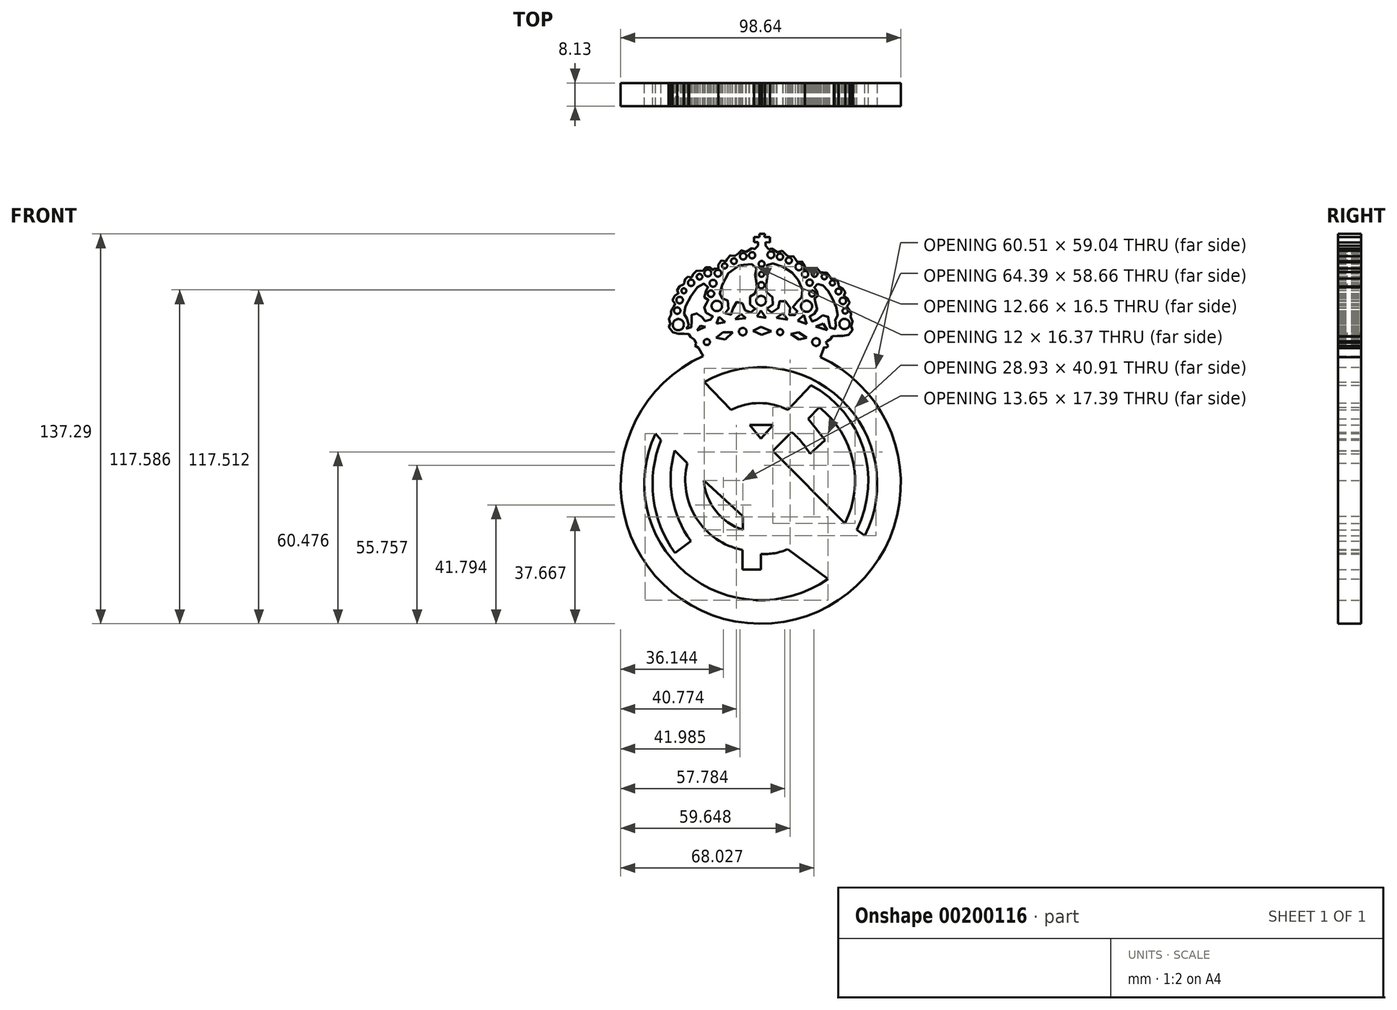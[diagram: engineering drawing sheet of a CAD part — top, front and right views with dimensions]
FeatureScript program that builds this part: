
annotation { "Feature Type Name" : "Feature", "Feature Type Description" : "" }
export const myFeature = defineFeature(function(context is Context, id is Id, definition is map)
    precondition{}
    {
        {
            var Q0;
            Q0=qCreatedBy(makeId("Front.planeOp"),FACE);
            var sketch = newSketch(context, id + "F0", { "sketchPlane" : qUnion([Q0])});
            skCircle(sketch, "E0", {"center": v(0, -1.17) * mm, "radius": 49.32 * mm});
            skCircle(sketch, "E1", {"center": v(0, -1.17) * mm, "radius": 41.02 * mm});
            skArc(sketch, "E2", {"start": v(-18.95, 33.67) * mm, "mid": v(-37.34, 6.45) * mm, "end": v(-30.16, -25.6) * mm});
            skArc(sketch, "E3", {"start": v(-19.8, 27.48) * mm, "mid": v(-31.53, 3.97) * mm, "end": v(-24.63, -21.38) * mm});
            skLineSegment(sketch, "E4", {"start": v(-19.8, 27.48) * mm, "end": v(-14.73, 21.41) * mm});
            skLineSegment(sketch, "E5", {"start": v(-18.95, 33.67) * mm, "end": v(-10.43, 24.82) * mm});
            skArc(sketch, "E6", {"start": v(-14.73, 21.41) * mm, "mid": v(-26.18, -4.34) * mm, "end": v(-6.47, -24.5) * mm});
            skLineSegment(sketch, "E7", {"start": v(-6.47, -24.5) * mm, "end": v(-6.47, -31.38) * mm});
            skLineSegment(sketch, "E8", {"start": v(-6.47, -31.38) * mm, "end": v(0, -31.38) * mm});
            skLineSegment(sketch, "E9", {"start": v(0, -31.38) * mm, "end": v(0, -25.92) * mm});
            skArc(sketch, "E10", {"start": v(0, -25.92) * mm, "mid": v(10.77, -23.7) * mm, "end": v(19, -16.42) * mm});
            skLineSegment(sketch, "E11", {"start": v(19, -16.42) * mm, "end": v(15.77, -12.98) * mm});
            skArc(sketch, "E12", {"start": v(0, -19.42) * mm, "mid": v(8.55, -17.84) * mm, "end": v(15.77, -12.98) * mm});
            skLineSegment(sketch, "E13", {"start": v(0, -19.42) * mm, "end": v(0, -13.17) * mm});
            skLineSegment(sketch, "E14", {"start": v(0, -13.17) * mm, "end": v(7.9, -13.17) * mm});
            skLineSegment(sketch, "E15", {"start": v(7.9, -13.17) * mm, "end": v(7.9, -8.88) * mm});
            skLineSegment(sketch, "E16", {"start": v(7.9, -8.88) * mm, "end": v(0, -8.88) * mm});
            skLineSegment(sketch, "E17", {"start": v(0, -8.88) * mm, "end": v(0, -3.61) * mm});
            skLineSegment(sketch, "E18", {"start": v(0, -3.61) * mm, "end": v(8.16, -3.61) * mm});
            skLineSegment(sketch, "E19", {"start": v(8.16, -3.61) * mm, "end": v(8.16, 0.94) * mm});
            skLineSegment(sketch, "E20", {"start": v(8.16, 0.94) * mm, "end": v(-6.35, 0.94) * mm});
            skLineSegment(sketch, "E21", {"start": v(-6.35, 0.94) * mm, "end": v(-6.35, -17.53) * mm});
            skArc(sketch, "E22", {"start": v(-11.49, 17.79) * mm, "mid": v(-19.81, -1.63) * mm, "end": v(-5.9, -17.53) * mm});
            skLineSegment(sketch, "E23", {"start": v(-11.49, 17.79) * mm, "end": v(0, 6.2) * mm});
            skLineSegment(sketch, "E24", {"start": v(0, 6.2) * mm, "end": v(10.89, 17) * mm});
            skArc(sketch, "E25", {"start": v(17.4, 9.33) * mm, "mid": v(14.45, 13.43) * mm, "end": v(10.89, 17) * mm});
            skLineSegment(sketch, "E26", {"start": v(17.4, 9.33) * mm, "end": v(22.73, 14.2) * mm});
            skLineSegment(sketch, "E27", {"start": v(22.73, 14.2) * mm, "end": v(16.74, 21.7) * mm});
            skLineSegment(sketch, "E28", {"start": v(16.74, 21.7) * mm, "end": v(20.65, 25.72) * mm});
            skLineSegment(sketch, "E29", {"start": v(-4.2, 19.87) * mm, "end": v(0, 14.73) * mm});
            skLineSegment(sketch, "E30", {"start": v(0, 14.73) * mm, "end": v(4.38, 19.54) * mm});
            skLineSegment(sketch, "E31", {"start": v(4.38, 19.54) * mm, "end": v(-3.94, 19.54) * mm});
            skArc(sketch, "E32", {"start": v(9.56, 24.82) * mm, "mid": v(-0.44, 27.23) * mm, "end": v(-10.43, 24.82) * mm});
            skLineSegment(sketch, "E33", {"start": v(9.56, 24.82) * mm, "end": v(17.72, 33.54) * mm});
            skArc(sketch, "E34", {"start": v(30.1, -23.34) * mm, "mid": v(36.99, 7.94) * mm, "end": v(17.72, 33.54) * mm});
            skLineSegment(sketch, "E35", {"start": v(30.1, -24) * mm, "end": v(26.4, -20.38) * mm});
            skLineSegment(sketch, "E36", {"start": v(30.1, -24) * mm, "end": v(30.1, -23.34) * mm});
            skArc(sketch, "E37", {"start": v(26.4, -20.38) * mm, "mid": v(32.95, 3.85) * mm, "end": v(20.65, 25.72) * mm});
            skLineSegment(sketch, "E38", {"start": v(-23.41, 49.61) * mm, "end": v(-20.3, 43.78) * mm});
            skArc(sketch, "E39", {"start": v(23.39, 49.61) * mm, "mid": v(-0.01, 54.78) * mm, "end": v(-23.41, 49.61) * mm});
            skLineSegment(sketch, "E40", {"start": v(23.39, 49.61) * mm, "end": v(21, 43.45) * mm});
            skCircle(sketch, "E41", {"center": v(-6.34, 52.39) * mm, "radius": 1.32 * mm});
            skCircle(sketch, "E42", {"center": v(6.84, 52.21) * mm, "radius": 1.06 * mm});
            skCircle(sketch, "E43", {"center": v(19.47, 48.72) * mm, "radius": 1.36 * mm});
            skCircle(sketch, "E44", {"center": v(-18.96, 48.72) * mm, "radius": 1.07 * mm});
            skLineSegment(sketch, "E45", {"start": v(-15.7, 50.27) * mm, "end": v(-13.28, 52.16) * mm});
            skLineSegment(sketch, "E46", {"start": v(-13.28, 52.16) * mm, "end": v(-9.81, 52.16) * mm});
            skLineSegment(sketch, "E47", {"start": v(-9.81, 52.16) * mm, "end": v(-12.48, 49.66) * mm});
            skLineSegment(sketch, "E48", {"start": v(-12.48, 49.66) * mm, "end": v(-15.7, 50.27) * mm});
            skLineSegment(sketch, "E49", {"start": v(-2.79, 52.65) * mm, "end": v(0, 54) * mm});
            skLineSegment(sketch, "E50", {"start": v(0, 54) * mm, "end": v(3.69, 52.55) * mm});
            skLineSegment(sketch, "E51", {"start": v(3.69, 52.55) * mm, "end": v(0.37, 51.28) * mm});
            skLineSegment(sketch, "E52", {"start": v(0.37, 51.28) * mm, "end": v(-2.79, 52.65) * mm});
            skLineSegment(sketch, "E53", {"start": v(10.66, 51.51) * mm, "end": v(13.3, 52.2) * mm});
            skLineSegment(sketch, "E54", {"start": v(13.3, 52.2) * mm, "end": v(16.15, 50.27) * mm});
            skLineSegment(sketch, "E55", {"start": v(16.15, 50.27) * mm, "end": v(13.51, 49.6) * mm});
            skLineSegment(sketch, "E56", {"start": v(13.51, 49.6) * mm, "end": v(10.66, 51.51) * mm});
            skLineSegment(sketch, "E57", {"start": v(21.74, 47.98) * mm, "end": v(22.72, 48.74) * mm});
            skLineSegment(sketch, "E58", {"start": v(22.72, 48.74) * mm, "end": v(23.77, 47.39) * mm});
            skLineSegment(sketch, "E59", {"start": v(23.77, 47.39) * mm, "end": v(22.77, 46.6) * mm});
            skLineSegment(sketch, "E60", {"start": v(22.77, 46.6) * mm, "end": v(21.74, 47.98) * mm});
            skLineSegment(sketch, "E61", {"start": v(-23.17, 47.48) * mm, "end": v(-22.33, 48.72) * mm});
            skLineSegment(sketch, "E62", {"start": v(-22.33, 48.72) * mm, "end": v(-21.23, 47.98) * mm});
            skLineSegment(sketch, "E63", {"start": v(-21.23, 47.98) * mm, "end": v(-21.85, 46.7) * mm});
            skLineSegment(sketch, "E64", {"start": v(-21.85, 46.7) * mm, "end": v(-23.17, 47.48) * mm});
            skFitSpline(sketch, "E65", {"points": [v(-23.41, 49.61) * mm, v(-24.63, 50.25) * mm, v(-24.83, 51.38) * mm, v(-26.15, 51.41) * mm, v(-27.74, 51.82) * mm, v(-29.91, 51.63) * mm, v(-31.74, 52.96) * mm, v(-32.4, 54.69) * mm, v(-31.7, 55.44) * mm, v(-32.37, 57.27) * mm, v(-31.39, 58.64) * mm, v(-31.58, 59.61) * mm, v(-31.25, 60.68) * mm, v(-30, 61.73) * mm, v(-30.35, 62.4) * mm, v(-31, 63.53) * mm, v(-30.36, 64.92) * mm, v(-29.07, 65.58) * mm, v(-29.1, 66.47) * mm, v(-29.42, 67.18) * mm, v(-28.47, 68.4) * mm, v(-27.42, 69.04) * mm, v(-27.31, 68.9) * mm, v(-27.11, 68.87) * mm, v(-27.02, 68.87) * mm, v(-27.07, 69.37) * mm, v(-27.04, 69.57) * mm, v(-26.93, 69.92) * mm, v(-26.85, 70.13) * mm, v(-26.72, 70.73) * mm, v(-26.55, 71) * mm, v(-26.24, 71.27) * mm, v(-26.14, 71.33) * mm, v(-25.83, 71.55) * mm, v(-25.5, 71.78) * mm, v(-25.46, 71.78) * mm], "startDerivative": vector(-42.62, 10.47) * mm, "endDerivative": vector(5.76, -0.88) * mm});
            skFitSpline(sketch, "E66", {"points": [v(-25.2, 71.6) * mm, v(-25, 71.53) * mm, v(-24.31, 71.49) * mm, v(-23.83, 72.47) * mm, v(-22.74, 73.75) * mm, v(-21.4, 73.87) * mm, v(-20.68, 73.53) * mm, v(-19.78, 74.75) * mm, v(-18.21, 75.08) * mm, v(-17.09, 74.48) * mm, v(-16.74, 73.92) * mm, v(-16.14, 74.72) * mm, v(-14.76, 74.54) * mm, v(-14.86, 76.46) * mm, v(-13.07, 77.5) * mm, v(-11.92, 77.2) * mm, v(-11.57, 78.58) * mm, v(-10.18, 79.29) * mm, v(-8.42, 79.14) * mm, v(-7.47, 80.76) * mm, v(-5.47, 80.74) * mm, v(-4.95, 80.38) * mm, v(-4.16, 81.2) * mm, v(-2.84, 81.66) * mm, v(-2.29, 81.4) * mm, v(-0.9, 82.66) * mm, v(-1.03, 82.88) * mm], "startDerivative": vector(9.59, -4.45) * mm, "endDerivative": vector(-13, 8.44) * mm});
            skLineSegment(sketch, "E67", {"start": v(0.46, 86.8) * mm, "end": v(-0.49, 86.8) * mm});
            skLineSegment(sketch, "E68", {"start": v(-0.49, 86.8) * mm, "end": v(-0.49, 85.74) * mm});
            skLineSegment(sketch, "E69", {"start": v(-0.49, 85.74) * mm, "end": v(-2.4, 85.74) * mm});
            skLineSegment(sketch, "E70", {"start": v(-2.4, 85.74) * mm, "end": v(-2.4, 83.88) * mm});
            skLineSegment(sketch, "E71", {"start": v(-2.4, 83.88) * mm, "end": v(-0.9, 83.88) * mm});
            skLineSegment(sketch, "E72", {"start": v(-0.9, 83.88) * mm, "end": v(-0.9, 82.66) * mm});
            skFitSpline(sketch, "E73.MirrorCS", {"points": [v(23.28, 48.95) * mm, v(24.5, 49.56) * mm, v(24.75, 50.67) * mm, v(26.07, 50.67) * mm, v(27.67, 51.03) * mm, v(29.83, 50.79) * mm, v(31.7, 52.06) * mm, v(32.4, 53.77) * mm, v(31.73, 54.54) * mm, v(32.45, 56.35) * mm, v(31.5, 57.75) * mm, v(31.73, 58.72) * mm, v(31.43, 59.8) * mm, v(30.2, 60.88) * mm, v(30.58, 61.53) * mm, v(31.26, 62.65) * mm, v(30.66, 64.06) * mm, v(29.38, 64.75) * mm, v(29.45, 65.64) * mm, v(29.78, 66.34) * mm, v(28.87, 67.6) * mm, v(27.84, 68.26) * mm, v(27.72, 68.12) * mm, v(27.52, 68.1) * mm, v(27.43, 68.1) * mm, v(27.49, 68.6) * mm, v(27.47, 68.8) * mm, v(27.37, 69.15) * mm, v(27.3, 69.36) * mm, v(27.18, 69.97) * mm, v(27.02, 70.24) * mm, v(26.71, 70.52) * mm, v(26.62, 70.58) * mm, v(26.31, 70.82) * mm, v(26, 71.05) * mm, v(25.95, 71.05) * mm], "startDerivative": vector(42.9, 9.26) * mm, "endDerivative": vector(-5.78, -0.72) * mm});
            skFitSpline(sketch, "E74.MirrorCS", {"points": [v(25.69, 70.89) * mm, v(25.48, 70.81) * mm, v(24.8, 70.79) * mm, v(24.34, 71.79) * mm, v(23.3, 73.1) * mm, v(21.95, 73.25) * mm, v(21.23, 72.94) * mm, v(20.36, 74.18) * mm, v(18.8, 74.56) * mm, v(17.66, 74) * mm, v(17.3, 73.44) * mm, v(16.72, 74.25) * mm, v(15.34, 74.11) * mm, v(15.49, 76.03) * mm, v(13.73, 77.13) * mm, v(12.57, 76.86) * mm, v(12.26, 78.24) * mm, v(10.9, 79) * mm, v(9.13, 78.9) * mm, v(8.22, 80.54) * mm, v(6.23, 80.57) * mm, v(5.7, 80.23) * mm, v(4.93, 81.07) * mm, v(3.63, 81.56) * mm, v(3.06, 81.33) * mm, v(1.72, 82.63) * mm, v(1.85, 82.84) * mm], "startDerivative": vector(-9.7, -4.18) * mm, "endDerivative": vector(13.23, 8.07) * mm});
            skLineSegment(sketch, "E75.MirrorCS", {"start": v(3.3, 85.66) * mm, "end": v(3.24, 83.8) * mm});
            skLineSegment(sketch, "E76.MirrorCS", {"start": v(1.75, 83.84) * mm, "end": v(1.72, 82.63) * mm});
            skLineSegment(sketch, "E77.MirrorCS", {"start": v(3.24, 83.8) * mm, "end": v(1.75, 83.84) * mm});
            skLineSegment(sketch, "E78.MirrorCS", {"start": v(1.39, 85.72) * mm, "end": v(3.3, 85.66) * mm});
            skLineSegment(sketch, "E79.MirrorCS", {"start": v(1.42, 86.78) * mm, "end": v(1.39, 85.72) * mm});
            skLineSegment(sketch, "E80.MirrorCS", {"start": v(0.46, 86.8) * mm, "end": v(1.42, 86.78) * mm});
            skCircle(sketch, "E81", {"center": v(-29, 54.84) * mm, "radius": 1.96 * mm});
            skCircle(sketch, "E82", {"center": v(-29.4, 59.77) * mm, "radius": 1.1 * mm});
            skCircle(sketch, "E83", {"center": v(-28.54, 63.5) * mm, "radius": 1.16 * mm});
            skCircle(sketch, "E84", {"center": v(-27.05, 66.77) * mm, "radius": 0.87 * mm});
            skCircle(sketch, "E85", {"center": v(-24.52, 69.58) * mm, "radius": 1.13 * mm});
            skCircle(sketch, "E86", {"center": v(-21.54, 71.7) * mm, "radius": 0.98 * mm});
            skCircle(sketch, "E87", {"center": v(-18.62, 73.02) * mm, "radius": 1.22 * mm});
            skCircle(sketch, "E88", {"center": v(-15.06, 72.96) * mm, "radius": 1.2 * mm});
            skCircle(sketch, "E89", {"center": v(-12.7, 75.54) * mm, "radius": 0.92 * mm});
            skCircle(sketch, "E90", {"center": v(-9.44, 77.2) * mm, "radius": 1 * mm});
            skCircle(sketch, "E91", {"center": v(-6.17, 78.93) * mm, "radius": 1.15 * mm});
            skCircle(sketch, "E92", {"center": v(-3.02, 79.27) * mm, "radius": 1.1 * mm});
            skCircle(sketch, "E93", {"center": v(-16.78, 69.4) * mm, "radius": 1.22 * mm});
            skCircle(sketch, "E94", {"center": v(-17.53, 65.73) * mm, "radius": 1.15 * mm});
            skCircle(sketch, "E95", {"center": v(-15.46, 61.43) * mm, "radius": 1.84 * mm});
            skCircle(sketch, "E96", {"center": v(0.13, 63.27) * mm, "radius": 1.7 * mm});
            skCircle(sketch, "E97", {"center": v(0.2, 68.72) * mm, "radius": 1.11 * mm});
            skCircle(sketch, "E98", {"center": v(0.26, 72.56) * mm, "radius": 0.9 * mm});
            skCircle(sketch, "E99", {"center": v(0.31, 76.23) * mm, "radius": 1.02 * mm});
            skCircle(sketch, "E100", {"center": v(16.14, 61.32) * mm, "radius": 1.96 * mm});
            skCircle(sketch, "E101", {"center": v(18.15, 65.8) * mm, "radius": 1.06 * mm});
            skCircle(sketch, "E102", {"center": v(17.23, 69.63) * mm, "radius": 1.11 * mm});
            skCircle(sketch, "E103", {"center": v(29.5, 55.07) * mm, "radius": 1.8 * mm});
            skCircle(sketch, "E104", {"center": v(29.73, 59.66) * mm, "radius": 0.95 * mm});
            skCircle(sketch, "E105", {"center": v(28.93, 63.21) * mm, "radius": 1.16 * mm});
            skCircle(sketch, "E106", {"center": v(27.38, 66.54) * mm, "radius": 1.03 * mm});
            skCircle(sketch, "E107", {"center": v(25.26, 69.52) * mm, "radius": 0.9 * mm});
            skCircle(sketch, "E108", {"center": v(22.4, 71.76) * mm, "radius": 0.94 * mm});
            skCircle(sketch, "E109", {"center": v(18.95, 72.73) * mm, "radius": 1.02 * mm});
            skCircle(sketch, "E110", {"center": v(3.58, 79.44) * mm, "radius": 1.2 * mm});
            skCircle(sketch, "E111", {"center": v(6.8, 78.75) * mm, "radius": 1.1 * mm});
            skCircle(sketch, "E112", {"center": v(9.89, 77.43) * mm, "radius": 1.08 * mm});
            skCircle(sketch, "E113", {"center": v(13.44, 75.2) * mm, "radius": 1.22 * mm});
            skFitSpline(sketch, "E114", {"points": [v(-26.19, 53.46) * mm, v(-24.4, 54.03) * mm, v(-24.4, 56.84) * mm, v(-23.9, 58.74) * mm, v(-21.14, 58.1) * mm, v(-19.88, 56.27) * mm, v(-18.39, 56.27) * mm, v(-16.67, 57.42) * mm, v(-19.65, 59.37) * mm, v(-19.76, 61.43) * mm, v(-19.02, 62.4) * mm, v(-18.44, 63.5) * mm, v(-19.76, 64.36) * mm, v(-19.07, 67.05) * mm, v(-18.56, 68.03) * mm, v(-20, 69.23) * mm, v(-24, 65.8) * mm, v(-27.05, 59.14) * mm, v(-26.07, 57.19) * mm, v(-25.44, 54.44) * mm, v(-26.19, 53.46) * mm]});
            skFitSpline(sketch, "E115", {"points": [v(-12.54, 58.9) * mm, v(-10.99, 58.16) * mm, v(-9.84, 59.66) * mm, v(-9.38, 61.9) * mm, v(-7.66, 63.04) * mm, v(-6.23, 61.95) * mm, v(-5.37, 59.77) * mm, v(-3.82, 59.02) * mm, v(-1.75, 60.11) * mm, v(-3.07, 61.03) * mm, v(-3.93, 63.15) * mm, v(-3.3, 65.33) * mm, v(-1.93, 65.85) * mm, v(-1.3, 67.63) * mm, v(-1.47, 69.92) * mm, v(-1.87, 71.13) * mm, v(-1.93, 73.08) * mm, v(-1.52, 74.8) * mm, v(-2.9, 76.06) * mm, v(-9.73, 74.62) * mm, v(-13.68, 68.32) * mm, v(-14.37, 65.28) * mm, v(-13.74, 64.07) * mm, v(-12.3, 64.01) * mm, v(-11.16, 61.66) * mm, v(-12.08, 59.25) * mm, v(-12.54, 58.9) * mm]});
            skFitSpline(sketch, "E116", {"points": [v(2.15, 60.46) * mm, v(3.75, 59.14) * mm, v(6.23, 60.8) * mm, v(6.68, 63.1) * mm, v(8.63, 63.1) * mm, v(10.35, 60.52) * mm, v(10.12, 58.16) * mm, v(11.95, 58.22) * mm, v(13.16, 59.25) * mm, v(11.38, 60.63) * mm, v(12.3, 62.4) * mm, v(13.96, 63.9) * mm, v(14.82, 65.9) * mm, v(13.16, 70.78) * mm, v(9.49, 74.28) * mm, v(3.8, 76.4) * mm, v(2.2, 75.77) * mm, v(2.49, 72.04) * mm, v(1.86, 66.7) * mm, v(3.87, 64.82) * mm, v(4.33, 62) * mm, v(2.15, 60.46) * mm]});
            skFitSpline(sketch, "E117", {"points": [v(19.98, 69.12) * mm, v(18.84, 67.86) * mm, v(19.75, 66.77) * mm, v(20.04, 64.82) * mm, v(18.84, 63.9) * mm, v(19.47, 62.12) * mm, v(19.52, 59.02) * mm, v(17.17, 57.75) * mm, v(18.43, 55.87) * mm, v(21.02, 57.75) * mm, v(23.65, 57.75) * mm, v(24.11, 54.84) * mm, v(24.75, 53.58) * mm, v(26.64, 53.58) * mm, v(26.07, 55.98) * mm, v(26.98, 57.75) * mm, v(25.6, 63.27) * mm, v(22.62, 68.03) * mm, v(19.98, 69.12) * mm]});
            skCircle(sketch, "E118", {"center": v(15.62, 72.62) * mm, "radius": 1.11 * mm});
            skLineSegment(sketch, "E119", {"start": v(-22.4, 52.77) * mm, "end": v(-21.23, 54.45) * mm});
            skLineSegment(sketch, "E120", {"start": v(-21.23, 54.45) * mm, "end": v(-19.47, 54.03) * mm});
            skLineSegment(sketch, "E121", {"start": v(-19.47, 54.03) * mm, "end": v(-22.4, 52.77) * mm});
            skLineSegment(sketch, "E122", {"start": v(-15.52, 55.24) * mm, "end": v(-14.67, 57.65) * mm});
            skLineSegment(sketch, "E123", {"start": v(-14.67, 57.65) * mm, "end": v(-12.48, 55.7) * mm});
            skLineSegment(sketch, "E124", {"start": v(-12.48, 55.7) * mm, "end": v(-15.52, 55.24) * mm});
            skLineSegment(sketch, "E125", {"start": v(-8.92, 56.73) * mm, "end": v(-6.86, 58.68) * mm});
            skLineSegment(sketch, "E126", {"start": v(-6.86, 58.68) * mm, "end": v(-5.33, 57.06) * mm});
            skLineSegment(sketch, "E127", {"start": v(-5.33, 57.06) * mm, "end": v(-8.92, 56.73) * mm});
            skLineSegment(sketch, "E128", {"start": v(5.46, 57.23) * mm, "end": v(7.83, 58.91) * mm});
            skLineSegment(sketch, "E129", {"start": v(7.83, 58.91) * mm, "end": v(9.52, 56.54) * mm});
            skLineSegment(sketch, "E130", {"start": v(9.52, 56.54) * mm, "end": v(5.46, 57.23) * mm});
            skLineSegment(sketch, "E131", {"start": v(13.07, 56.27) * mm, "end": v(15.2, 58.23) * mm});
            skLineSegment(sketch, "E132", {"start": v(15.2, 58.23) * mm, "end": v(16.2, 55.14) * mm});
            skLineSegment(sketch, "E133", {"start": v(16.2, 55.14) * mm, "end": v(13.38, 56.14) * mm});
            skLineSegment(sketch, "E134", {"start": v(13.38, 56.14) * mm, "end": v(13.07, 56.27) * mm});
            skLineSegment(sketch, "E135", {"start": v(-1.34, 57.77) * mm, "end": v(0.08, 59.83) * mm});
            skLineSegment(sketch, "E136", {"start": v(0.08, 59.83) * mm, "end": v(1.84, 57.23) * mm});
            skLineSegment(sketch, "E137", {"start": v(1.84, 57.23) * mm, "end": v(-1.34, 57.77) * mm});
            skLineSegment(sketch, "E138", {"start": v(19.37, 54.2) * mm, "end": v(22.04, 55.15) * mm});
            skLineSegment(sketch, "E139", {"start": v(22.04, 55.15) * mm, "end": v(23.37, 52.96) * mm});
            skLineSegment(sketch, "E140", {"start": v(23.37, 52.96) * mm, "end": v(19.37, 54.2) * mm});
            skLineSegment(sketch, "E141", {"start": v(4.73, 9.92) * mm, "end": v(28.45, -13.98) * mm});
            skLineSegment(sketch, "E142", {"start": v(28.45, -13.98) * mm, "end": v(29.65, -15.19) * mm});
            skLineSegment(sketch, "E143", {"start": v(30.6, -25.47) * mm, "end": v(30.1, -24) * mm});
            skLineSegment(sketch, "E144", {"start": v(-30.3, 10.47) * mm, "end": v(-25.87, 6.01) * mm});
            skLineSegment(sketch, "E145", {"start": v(-20, 0) * mm, "end": v(-6.35, -12.56) * mm});
            skLineSegment(sketch, "E146", {"start": v(23.28, 48.95) * mm, "end": v(23.13, 48.94) * mm});
            skLineSegment(sketch, "E147", {"start": v(-25.46, 71.78) * mm, "end": v(-25.2, 71.6) * mm});
            skLineSegment(sketch, "E148", {"start": v(25.69, 70.89) * mm, "end": v(25.95, 71.05) * mm});
            skLineSegment(sketch, "E149", {"start": v(4.73, 9.92) * mm, "end": v(4.24, 10.42) * mm});
            skLineSegment(sketch, "E150", {"start": v(-30.16, -25.6) * mm, "end": v(-24.63, -21.38) * mm});
            skLineSegment(sketch, "E151", {"start": v(30.6, -25.47) * mm, "end": v(32.02, -26.8) * mm});
            skLineSegment(sketch, "E152", {"start": v(-35.07, 14.2) * mm, "end": v(-37.01, 16.5) * mm});
            skLineSegment(sketch, "E153", {"start": v(-18.95, 33.67) * mm, "end": v(-19.92, 34.68) * mm});
            skLineSegment(sketch, "E154", {"start": v(10.77, -25.15) * mm, "end": v(23.65, -34.7) * mm});
            skPoint(sketch, "E154.startSnap0", {"position": v(10.77, -23.7) * mm});
            skLineSegment(sketch, "E155", {"start": v(10.77, -25.15) * mm, "end": v(9.57, -24.26) * mm});
            skLineSegment(sketch, "E156", {"start": v(33.8, -17.39) * mm, "end": v(36.68, -19.53) * mm});
            skSolve(sketch);
        }
        {
            var Q0;
            Q0 = qSketchRegion(id + "F0", true);
            var Q1;
            {var subQ10=sQuery(id+"F0.wireOp",EDGE,"E11");Q1=makeQuery(id+"F0.imprint","IMPRINT",FACE,{"disambiguationData":[TD([[makeQuery(id+"F0.imprint","IMPRINT",EDGE,{"derivedFrom":subQ10}),-1.0]])]});}
            var Q2;
            {var subQ13=sQuery(id+"F0.wireOp",EDGE,"E4");Q2=makeQuery(id+"F0.imprint","IMPRINT",FACE,{"disambiguationData":[TD([[makeQuery(id+"F0.imprint","IMPRINT",EDGE,{"derivedFrom":subQ13}),1.0]])]});}
            var Q3;
            {var subQ0=sQuery(id+"F0.wireOp",EDGE,"E4");Q3=makeQuery(id+"F0.imprint","IMPRINT",FACE,{"disambiguationData":[TD([[makeQuery(id+"F0.imprint","IMPRINT",EDGE,{"derivedFrom":subQ0}),-1.0]])]});}
            var Q4;
            {var subQ0=sQuery(id+"F0.wireOp",EDGE,"E152");Q4=makeQuery(id+"F0.imprint","IMPRINT",FACE,{"disambiguationData":[TD([[makeQuery(id+"F0.imprint","IMPRINT",EDGE,{"derivedFrom":subQ0}),-1.0]])]});}
            var Q5;
            {var subQ0=sQuery(id+"F0.wireOp",EDGE,"E36");Q5=makeQuery(id+"F0.imprint","IMPRINT",FACE,{"disambiguationData":[TD([[makeQuery(id+"F0.imprint","IMPRINT",EDGE,{"derivedFrom":subQ0}),-1.0]])]});}
            extrude(context, id + "F1", {"entities" : qUnion([Q0, Q1, Q2, Q3, Q4, Q5]), "depth" : 8.13 * mm});
        }
    });
